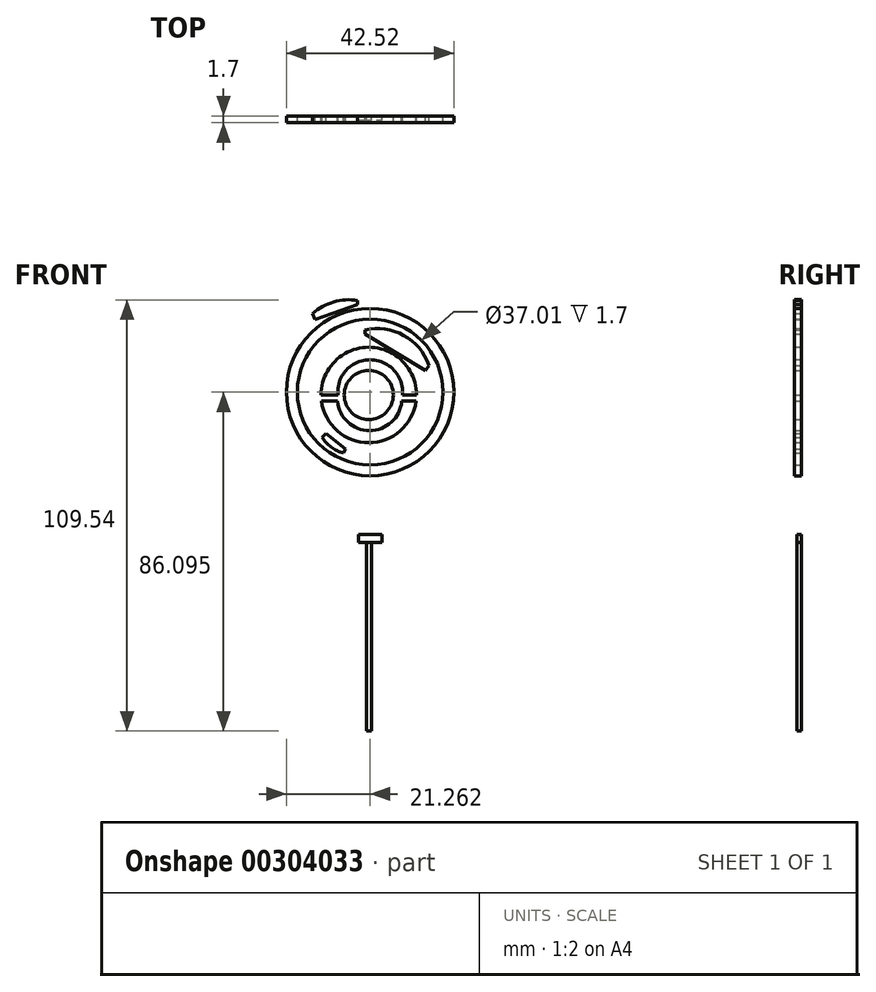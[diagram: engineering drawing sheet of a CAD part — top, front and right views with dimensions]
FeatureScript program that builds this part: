
annotation { "Feature Type Name" : "Feature", "Feature Type Description" : "" }
export const myFeature = defineFeature(function(context is Context, id is Id, definition is map)
    precondition{}
    {
        {
            var Q0;
            Q0=qCreatedBy(makeId("Front.planeOp"),FACE);
            var sketch = newSketch(context, id + "F0", { "sketchPlane" : qUnion([Q0])});
            skArc(sketch, "E0", {"start": v(-12.01, 15.07) * mm, "mid": v(0, 4.54) * mm, "end": v(12.01, 15.07) * mm});
            skLineSegment(sketch, "E1", {"start": v(-12.12, 16.63) * mm, "end": v(-7.83, 16.63) * mm});
            skLineSegment(sketch, "E2", {"start": v(-12.01, 15.07) * mm, "end": v(-7.94, 15.07) * mm});
            skArc(sketch, "E3.trimOffspring", {"start": v(12.12, 16.63) * mm, "mid": v(0, 28.78) * mm, "end": v(-12.12, 16.63) * mm});
            skLineSegment(sketch, "E4.trimOffspring", {"start": v(8.54, 16.63) * mm, "end": v(12.12, 16.63) * mm});
            skLineSegment(sketch, "E5.trimOffspring", {"start": v(8.37, 15.07) * mm, "end": v(12.01, 15.07) * mm});
            skCircle(sketch, "E6", {"center": v(0, 16.66) * mm, "radius": 6.23 * mm});
            skArc(sketch, "E7", {"start": v(8.54, 16.63) * mm, "mid": v(0.35, 25.61) * mm, "end": v(-7.83, 16.63) * mm});
            skArc(sketch, "E8", {"start": v(-7.94, 15.07) * mm, "mid": v(0.22, 7.6) * mm, "end": v(8.37, 15.07) * mm});
            skArc(sketch, "E9", {"start": v(-11.9, 5.91) * mm, "mid": v(-9.52, 3.4) * mm, "end": v(-6.4, 1.9) * mm});
            skLineSegment(sketch, "E10", {"start": v(-6.4, 1.9) * mm, "end": v(-5.85, 3) * mm});
            skLineSegment(sketch, "E11", {"start": v(-5.85, 3) * mm, "end": v(-10.88, 6.83) * mm});
            skLineSegment(sketch, "E12", {"start": v(-10.88, 6.83) * mm, "end": v(-11.9, 5.91) * mm});
            skArc(sketch, "E13", {"start": v(-2.8, 40.69) * mm, "mid": v(-8.9, 40.28) * mm, "end": v(-14.27, 37.37) * mm});
            skLineSegment(sketch, "E14", {"start": v(-2.8, 40.69) * mm, "end": v(-2.8, 39.7) * mm});
            skLineSegment(sketch, "E15", {"start": v(-2.8, 39.7) * mm, "end": v(-13.62, 35.87) * mm});
            skLineSegment(sketch, "E16", {"start": v(-13.62, 35.87) * mm, "end": v(-14.27, 37.37) * mm});
            skArc(sketch, "E17", {"start": v(15.3, 24.2) * mm, "mid": v(8.87, 31.79) * mm, "end": v(-0.98, 33.18) * mm});
            skLineSegment(sketch, "E18", {"start": v(15.3, 24.2) * mm, "end": v(14.4, 22.92) * mm});
            skLineSegment(sketch, "E19", {"start": v(14.4, 22.92) * mm, "end": v(-0.98, 32.1) * mm});
            skLineSegment(sketch, "E20", {"start": v(-0.98, 32.1) * mm, "end": v(-0.98, 33.18) * mm});
            skLineSegment(sketch, "E21", {"start": v(12.25, 24.2) * mm, "end": v(13.1, 25.61) * mm});
            skPoint(sketch, "E21.endSnap0", {"position": v(0.35, 25.61) * mm});
            skCircle(sketch, "E22", {"center": v(0.35, 17.4) * mm, "radius": 18.5 * mm});
            skCircle(sketch, "E23", {"center": v(0.35, 17.4) * mm, "radius": 21.26 * mm});
            skSolve(sketch);
        }
        {
            var Q0;
            Q0 = qSketchRegion(id + "F0", true);
            var Q1;
            Q1=makeQuery(id+"F0.imprint","IMPRINT",FACE,{"disambiguationData":[TD([[makeQuery(id+"F0.imprint","IMPRINT",EDGE,{"derivedFrom":sQuery(id+"F0.wireOp",EDGE,"E1")}),1.0]])]});
            var Q2;
            Q2=makeQuery(id+"F0.imprint","IMPRINT",FACE,{"disambiguationData":[TD([[makeQuery(id+"F0.imprint","IMPRINT",EDGE,{"derivedFrom":sQuery(id+"F0.wireOp",EDGE,"E0")}),1.0]])]});
            var Q3;
            Q3=makeQuery(id+"F0.imprint","IMPRINT",FACE,{"disambiguationData":[TD([[makeQuery(id+"F0.imprint","IMPRINT",EDGE,{"derivedFrom":sQuery(id+"F0.wireOp",EDGE,"E6")}),1.0]])]});
            var Q4;
            Q4=makeQuery(id+"F0.imprint","IMPRINT",FACE,{"disambiguationData":[TD([[makeQuery(id+"F0.imprint","IMPRINT",EDGE,{"derivedFrom":sQuery(id+"F0.wireOp",EDGE,"E17")}),1.0]])]});
            var Q5;
            Q5=makeQuery(id+"F0.imprint","IMPRINT",FACE,{"disambiguationData":[TD([[makeQuery(id+"F0.imprint","IMPRINT",EDGE,{"derivedFrom":sQuery(id+"F0.wireOp",EDGE,"E9")}),1.0]])]});
            extrude(context, id + "F1", {"entities" : qUnion([Q0, Q1, Q2, Q3, Q4, Q5]), "depth" : 1.7 * mm});
        }
        {
            var Q0;
            Q0=qCreatedBy(makeId("Front.planeOp"),FACE);
            var sketch = newSketch(context, id + "F2", { "sketchPlane" : qUnion([Q0])});
            skLineSegment(sketch, "E24", {"start": v(-2.64, -18.83) * mm, "end": v(-2.64, -20.86) * mm});
            skLineSegment(sketch, "E25", {"start": v(-2.64, -20.86) * mm, "end": v(3.36, -20.83) * mm});
            skLineSegment(sketch, "E26", {"start": v(-2.64, -18.83) * mm, "end": v(3.36, -18.83) * mm});
            skLineSegment(sketch, "E27", {"start": v(3.36, -18.83) * mm, "end": v(3.36, -20.83) * mm});
            skLineSegment(sketch, "E28", {"start": v(0, -65.13) * mm, "end": v(0, 65.62) * mm, "construction": true});
            skLineSegment(sketch, "E29.bottom", {"start": v(-0.55, -20.85) * mm, "end": v(0.76, -20.85) * mm});
            skLineSegment(sketch, "E29.top", {"start": v(-0.55, -68.7) * mm, "end": v(0.76, -68.7) * mm});
            skLineSegment(sketch, "E29.left", {"start": v(-0.55, -20.85) * mm, "end": v(-0.55, -68.7) * mm});
            skLineSegment(sketch, "E29.right", {"start": v(0.76, -20.85) * mm, "end": v(0.76, -68.7) * mm});
            skSolve(sketch);
        }
        {
            var Q0;
            Q0=makeQuery(id+"F2.imprint","IMPRINT",FACE,{"disambiguationData":[TD([[makeQuery(id+"F2.imprint","IMPRINT",EDGE,{"derivedFrom":sQuery(id+"F2.wireOp",EDGE,"E29.bottom")}),-1.0]])]});
            var Q1;
            {var subQ3=sQuery(id+"F2.wireOp",EDGE,"E24");Q1=makeQuery(id+"F2.imprint","IMPRINT",FACE,{"disambiguationData":[TD([[makeQuery(id+"F2.imprint","IMPRINT",EDGE,{"derivedFrom":subQ3}),1.0]])]});}
            extrude(context, id + "F3", {"entities" : qUnion([Q0, Q1]), "depth" : 1.1 * mm});
        }
        {
            var Q0;
            Q0=qCreatedBy(makeId("Top.planeOp"),FACE);
            cPlane(context, id + "F4", {"entities" : qUnion([Q0]), "cplaneType" : CPlaneType.OFFSET, "offset" : 68.5 * mm, "oppositeDirection" : true, "width" : 150 * mm, "height" : 150 * mm});
        }
    });
